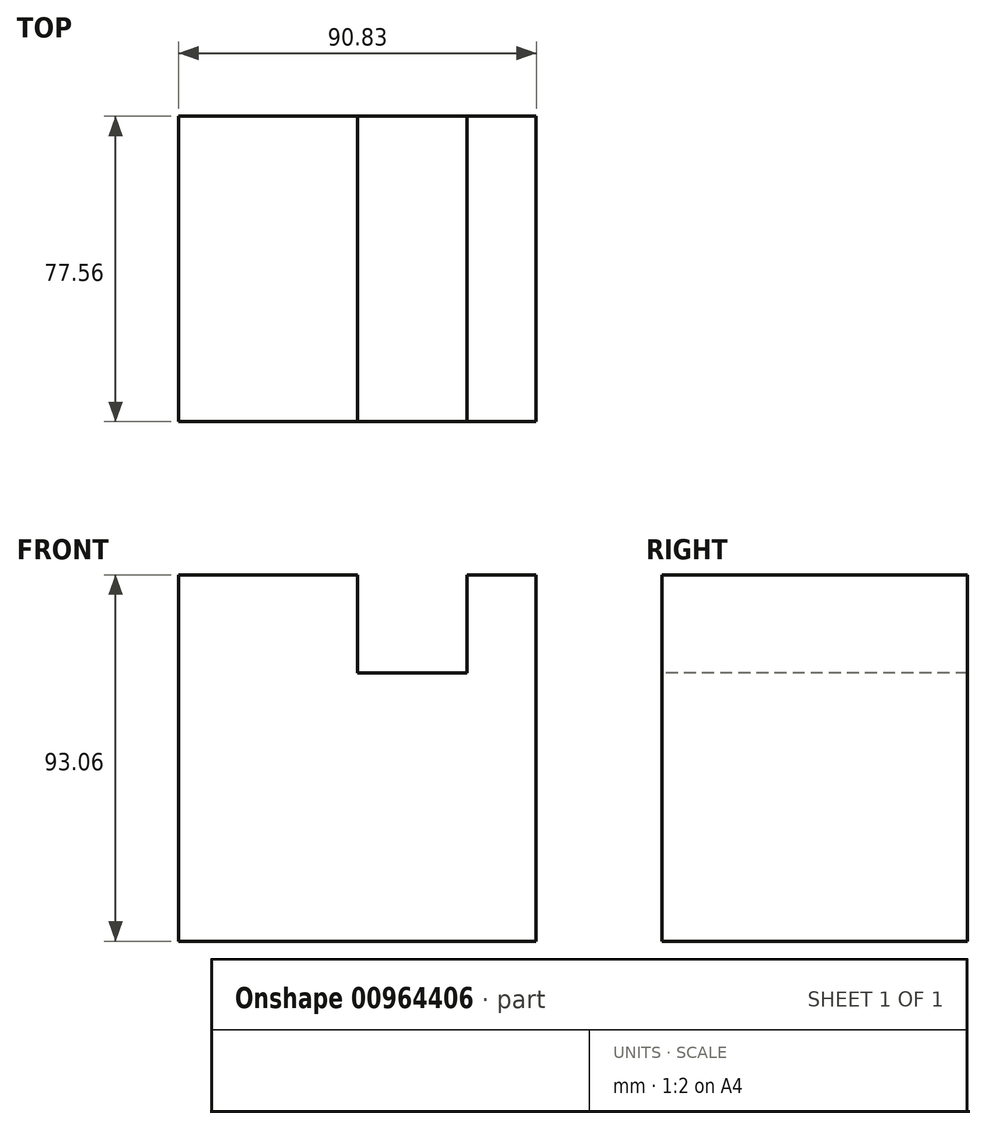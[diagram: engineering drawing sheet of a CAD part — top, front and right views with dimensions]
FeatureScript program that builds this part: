
annotation { "Feature Type Name" : "Feature", "Feature Type Description" : "" }
export const myFeature = defineFeature(function(context is Context, id is Id, definition is map)
    precondition{}
    {
        {
            var Q0;
            Q0=qCreatedBy(makeId("Top.planeOp"),FACE);
            var sketch = newSketch(context, id + "F0", { "sketchPlane" : qUnion([Q0])});
            skLineSegment(sketch, "E0.bottom", {"start": v(-69.7, 26.42) * mm, "end": v(21.13, 26.42) * mm});
            skLineSegment(sketch, "E0.top", {"start": v(-69.7, -51.14) * mm, "end": v(21.13, -51.14) * mm});
            skLineSegment(sketch, "E0.left", {"start": v(-69.7, 26.42) * mm, "end": v(-69.7, -51.14) * mm});
            skLineSegment(sketch, "E0.right", {"start": v(21.13, 26.42) * mm, "end": v(21.13, -51.14) * mm});
            skSolve(sketch);
        }
        {
            var Q0;
            Q0 = qSketchRegion(id + "F0", true);
            extrude(context, id + "F1", {"entities" : qUnion([Q0]), "depth" : 93.06 * mm, "offsetDistance" : 25 * mm});
        }
        {
            var Q0;
            Q0=makeQuery(id+"F1.opExtrude","SWEPT_FACE",FACE,{"disambiguationData":[OSD([sQuery(id+"F0.wireOp",EDGE,"E0.top")])]});
            var sketch = newSketch(context, id + "F2", { "sketchPlane" : qUnion([Q0])});
            skLineSegment(sketch, "E1.bottom", {"start": v(-24.29, 68.19) * mm, "end": v(3.5, 68.19) * mm});
            skLineSegment(sketch, "E1.top", {"start": v(-24.29, 104.46) * mm, "end": v(3.5, 104.46) * mm});
            skLineSegment(sketch, "E1.left", {"start": v(-24.29, 68.19) * mm, "end": v(-24.29, 104.46) * mm});
            skLineSegment(sketch, "E1.right", {"start": v(3.5, 68.19) * mm, "end": v(3.5, 104.46) * mm});
            skPoint(sketch, "E1.middle", {"position": v(-10.4, 86.32) * mm});
            skPoint(sketch, "E1.cornerSnap0", {"position": v(-24.29, 93.06) * mm});
            skSolve(sketch);
        }
        {
            var Q0;
            {var subQ0=sQuery(id+"F2.wireOp",EDGE,"E1.bottom");Q0=makeQuery(id+"F2.imprint","IMPRINT",FACE,{"disambiguationData":[TD([[makeQuery(id+"F2.imprint","IMPRINT",EDGE,{"derivedFrom":subQ0}),1.0]])]});}
            extrude(context, id + "F3", {"entities" : qUnion([Q0]), "operationType" : NewBodyOperationType.REMOVE, "oppositeDirection" : true, "depth" : 143.12 * mm, "offsetDistance" : 25 * mm});
        }
    });
